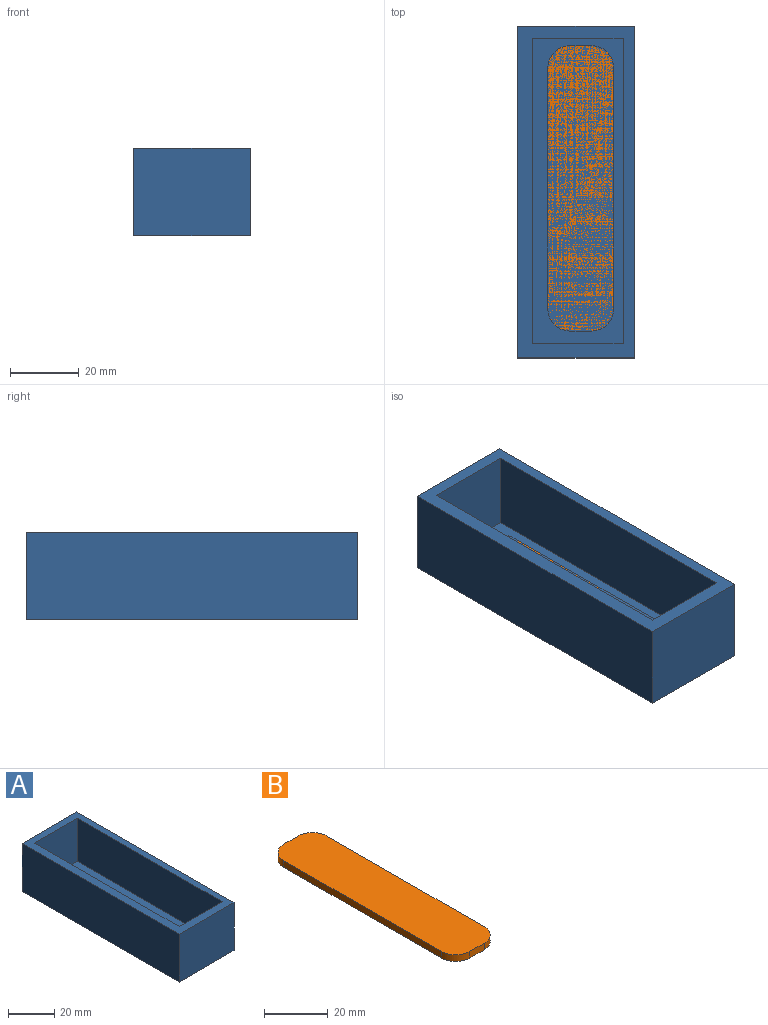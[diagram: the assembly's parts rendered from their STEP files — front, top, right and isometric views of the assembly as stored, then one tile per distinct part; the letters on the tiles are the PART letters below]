
ASSEMBLY  parts=2 mates=1
PART A: 11 faces, bbox 33.7x96.3x25.4 mm
  f0: plane 96.29x33.69mm, normal (0,0,1), area 905mm2, adj f1,f2,f3,f4,f6,f7,f8,f9
  f1: plane 33.69x25.4mm, normal (0,1,0), area 855.6mm2, adj f0,f2,f4,f5
  f2: plane 96.29x25.4mm, normal (-1,0,0), area 2445.8mm2, adj f0,f1,f3,f5
  f3: plane 33.69x25.4mm, normal (0,-1,0), area 855.6mm2, adj f0,f2,f4,f5
  f4: plane 96.29x25.4mm, normal (1,0,0), area 2445.8mm2, adj f0,f1,f3,f5
  f5: plane 96.29x33.69mm, normal (0,0,-1), area 3243.6mm2, adj f1,f2,f3,f4
  f6: plane 26.38x22.86mm, normal (0,-1,0), area 603mm2, adj f0,f7,f9,f10
  f7: plane 88.66x22.86mm, normal (1,0,0), area 2026.9mm2, adj f0,f6,f8,f10
  f8: plane 26.38x22.86mm, normal (0,1,0), area 603mm2, adj f0,f7,f9,f10
  f9: plane 88.66x22.86mm, normal (-1,0,0), area 2026.9mm2, adj f0,f6,f8,f10
  f10: plane 88.66x26.38mm, normal (0,0,1), area 2338.7mm2, adj f6,f7,f8,f9
PART B: 10 faces, bbox 19.1x82.8x2.5 mm
  f0: plane 6.38x2.54mm, normal (0,-1,0), area 16.2mm2, adj f1,f7,f8,f9
  f1: cylinder r=6.35mm len=6.35mm, axis (0,0,-1), area 25.3mm2, adj f0,f2,f8,f9
  f2: plane 70.09x2.54mm, normal (1,0,0), area 178mm2, adj f1,f3,f8,f9
  f3: cylinder r=6.35mm len=6.35mm, axis (0,0,-1), area 25.3mm2, adj f2,f4,f8,f9
  f4: plane 6.38x2.54mm, normal (0,1,0), area 16.2mm2, adj f3,f5,f8,f9
  f5: cylinder r=6.35mm len=6.35mm, axis (0,0,-1), area 25.3mm2, adj f4,f6,f8,f9
  f6: plane 70.09x2.54mm, normal (-1,0,0), area 178mm2, adj f5,f7,f8,f9
  f7: cylinder r=6.35mm len=6.35mm, axis (0,0,-1), area 25.3mm2, adj f0,f6,f8,f9
  f8: plane 82.79x19.08mm, normal (0,0,1), area 1544.6mm2, adj f0,f1,f2,f3,f4,f5,f6,f7
  f9: plane 82.79x19.08mm, normal (0,0,-1), area 1544.6mm2, adj f0,f1,f2,f3,f4,f5,f6,f7
PLACE A t=(-25.07,-38.47,-1.16)mm
PLACE B t=(-88.72,-50.64,-1.16)mm
MATE planar B.f8 <-> A.f10  axis (0,0,-1) through (-55.23,-75.31,1.38)mm
